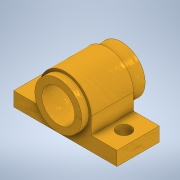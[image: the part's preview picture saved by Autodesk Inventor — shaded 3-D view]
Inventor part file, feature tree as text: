
AUTODESK INVENTOR PART (.ipt)
format: ipt  version: 2020 (Build 240168000, 168)  size: 176,128 bytes
history: native  units: mm
features: sketch x8, extrude x7, hole x1
ambient origin geometry x8: Origin, YZ Plane, XZ Plane, XY Plane, X Axis, Y Axis, Z Axis, Center Point
bodies: Solid1 (feature_tree)
feature tree (16):
  extrude  "Extrusion1"  Depth=9.0mm
  extrude  "Extrusion2"  Depth=11.0mm
  extrude  "Extrusion3"  TaperAngle=0.0deg  [1 undecoded]
  extrude  "Extrusion4"  Depth=9.0mm TaperAngle=0.0deg
  extrude  "Extrusion5"  Depth=10.0mm
  extrude  "Extrusion6"  Depth=10.0mm
  extrude  "Extrusion7"  Depth=7.0mm
  hole  "Hole1"  [1 undecoded]
  sketch  "Sketch1"  dims[d0=22.0mm d1=9.0mm]
  sketch  "Sketch2"  dims[d2=3.0mm d3=0.0mm d4=11.0mm]
  sketch  "Sketch3"  dims[d5=9.0mm d6=0.0mm]
  sketch  "Sketch4"  dims[d7=5.5mm d8=9.0mm d9=0.0mm]
  sketch  "Sketch5"  dims[d10=10.0mm d11=5.5mm]
  sketch  "Sketch6"  dims[d12=1.5mm d13=0.0mm d14=10.0mm]
  sketch  "Sketch7"  dims[d15=3.0mm d16=0.0mm d17=7.0mm]
  sketch  "Sketch8"  dims[d18=0.0mm d19=0.0mm d20=3.0mm d21=3.0mm d22=0.0mm d23=0.0mm d24=3.0mm d25=3.0mm d26=0.0mm d27=0.0mm d28=3.0mm d29=1.0mm d30=6.0mm d31=3.0mm d32=2.0mm d33=90.0deg d34=3.04mm d35=20.594885mm]
note: 2 required parameter values undecoded (feature->parameter linkage not recoverable at this tier; creation-order binding heuristic only, values carry confidence <= 0.55)
